# Revit family: Manifold Bracket Assy-JCI_Sapphire_Plus-(70 bar)Novec1
name_source: partatom
category: Specialty Equipment
revit_build: Autodesk Revit 2017 (Build: 20171027_0315(x64)
units: mm (PartAtom-declared; Revit-internal decimal feet)

## family parameters
Always vertical = No
Cut with Voids When Loaded = No
OmniClass Number = 23.29.33.13.11
Part Type = Normal
Room Calculation Point = No
Round Connector Dimension = Use Diameter
Shared = No
Work Plane-Based = Yes

## types (1)
- 150mm (6 in) Double Profile 2
    Cantilever Bracket Length = 300 mm  [stored 0.984252 ft]
    Cantilever Bracket Length ref = 460 mm  [stored 1.50919 ft]
    Cantilever Bracket Profile Height = 80 mm  [stored 0.262467 ft]
    Date Modified = YYYY/MM/DD
    Default Elevation = 0 mm  [stored 0 ft]
    Description = 150mm (6 in) Double Profile
    Equipment Abbreviation = MBR
    Equipment Number = XXX
    Family Version = 1.0
    Fire Suppression Agent = ''3M Novec'' 1230 Fire Protection Fluid
    Height = 50 mm  [stored 0.164042 ft]
    Length = 47.6 mm  [stored 0.156168 ft]
    Manufacturer = Johnson Controls, Inc.
    Material = JCI - Metal - Brass - Satin
    Model = 311700001
    Model Disclaimer = For More Information Contact JOHNSON CONTROLS
    Operating Temperature = 122 °F
    Part Description = 150mm (6 in) Double Profile
    Part Number = 311700001
    Pipe Clamp Radius = 75 mm
    Product Documentation Link = http://www.sapphireplus.com
    Product Material = JCI - Iron - Gray; JCI - Plastic - Red - Matte
    Product Page URL = http://www.sapphireplus.com
    URL = http://www.sapphireplus.com
    Unistrut Channel Length = 500 mm  [stored 1.64042 ft]
    Weight = 0.00 lbf
    Width = 47.6 mm  [stored 0.156168 ft]

note: [stored X ft] marks values corroborated as IEEE doubles in the binary element streams (Revit-internal decimal feet)

## geometry (parser evidence)
native form markers: Sweep x3
no freeform markers — native parametric forms only
